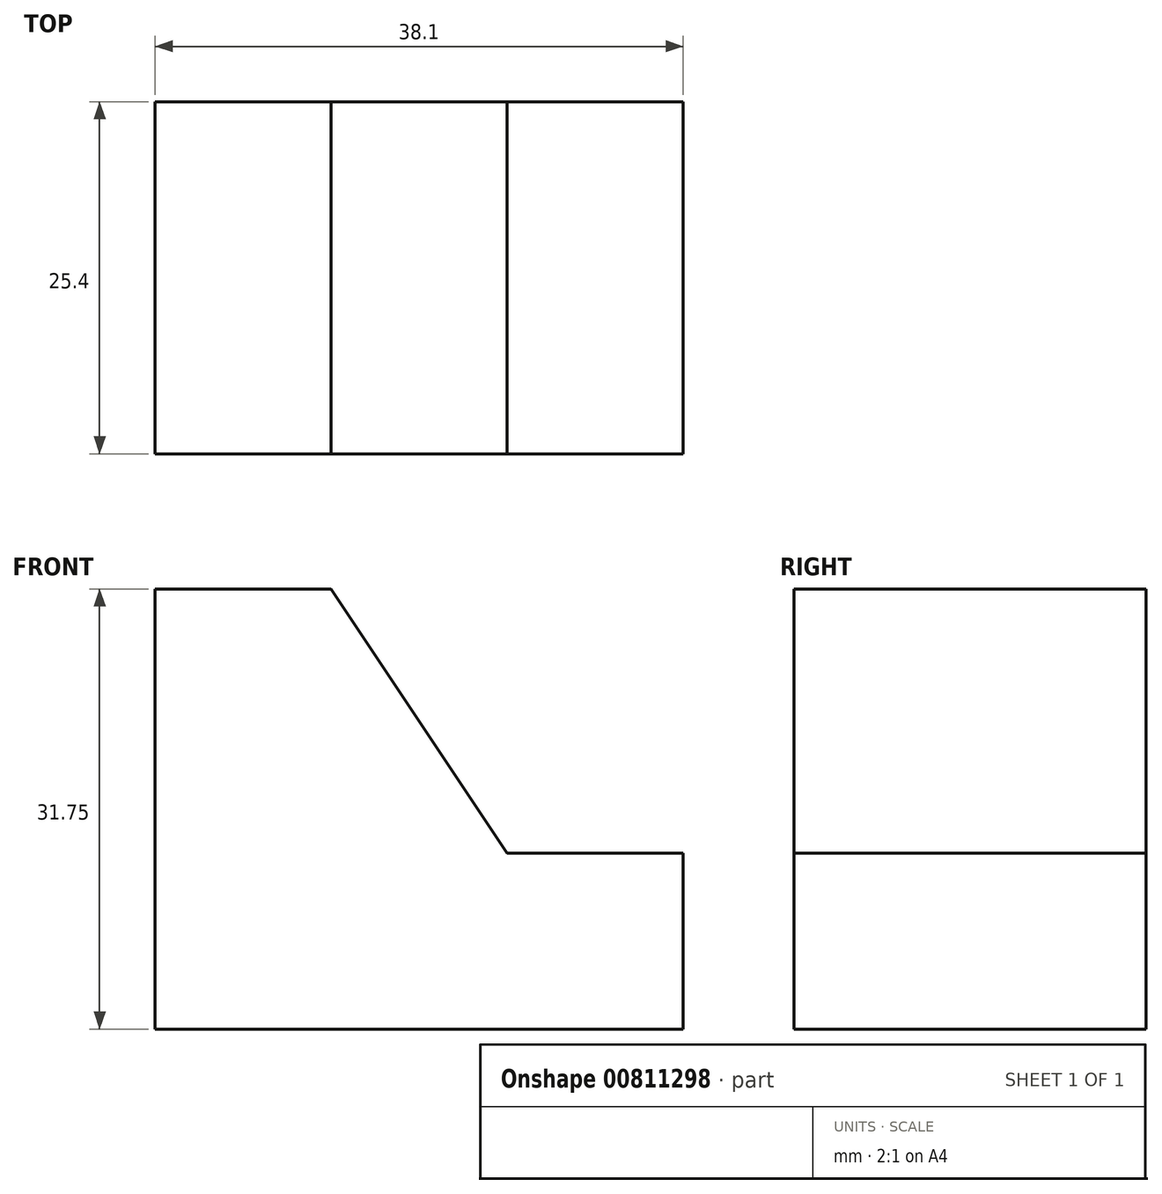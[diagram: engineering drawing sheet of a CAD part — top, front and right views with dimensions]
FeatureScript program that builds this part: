
annotation { "Feature Type Name" : "Feature", "Feature Type Description" : "" }
export const myFeature = defineFeature(function(context is Context, id is Id, definition is map)
    precondition{}
    {
        {
            var Q0;
            Q0=qCreatedBy(makeId("Front.planeOp"),FACE);
            var sketch = newSketch(context, id + "F0", { "sketchPlane" : qUnion([Q0])});
            skLineSegment(sketch, "E0", {"start": v(0, 0) * mm, "end": v(0, 31.75) * mm});
            skLineSegment(sketch, "E1", {"start": v(0, 31.75) * mm, "end": v(12.7, 31.75) * mm});
            skLineSegment(sketch, "E2", {"start": v(0, 0) * mm, "end": v(38.1, 0) * mm});
            skLineSegment(sketch, "E3", {"start": v(38.1, 0) * mm, "end": v(38.1, 12.7) * mm});
            skLineSegment(sketch, "E4", {"start": v(38.1, 12.7) * mm, "end": v(25.4, 12.7) * mm});
            skLineSegment(sketch, "E5", {"start": v(25.4, 12.7) * mm, "end": v(12.7, 31.75) * mm});
            skSolve(sketch);
        }
        {
            var Q0;
            Q0 = qSketchRegion(id + "F0", true);
            extrude(context, id + "F1", {"entities" : qUnion([Q0]), "depth" : 25.4 * mm, "offsetDistance" : 25.4 * mm});
        }
    });
